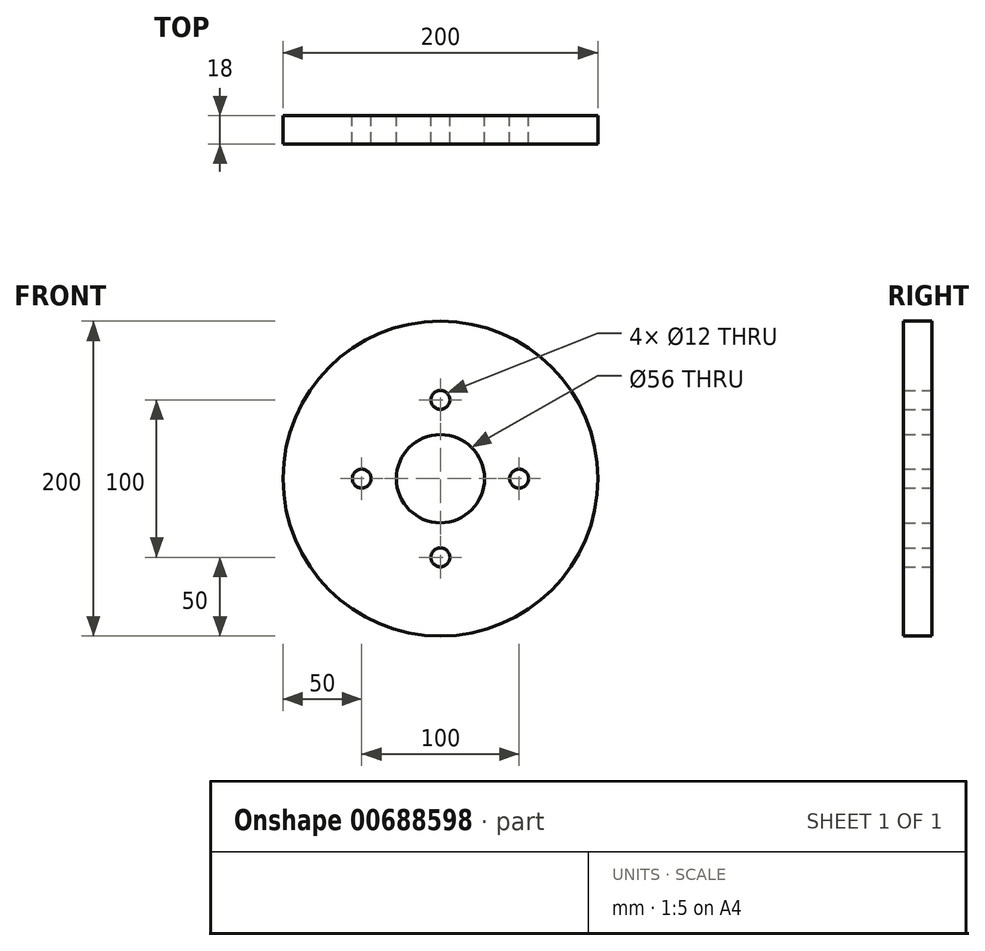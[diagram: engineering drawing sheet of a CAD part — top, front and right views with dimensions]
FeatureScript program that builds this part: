
annotation { "Feature Type Name" : "Feature", "Feature Type Description" : "" }
export const myFeature = defineFeature(function(context is Context, id is Id, definition is map)
    precondition{}
    {
        {
            var Q0;
            Q0=qCreatedBy(makeId("Front.planeOp"),FACE);
            var sketch = newSketch(context, id + "F0", { "sketchPlane" : qUnion([Q0])});
            skCircle(sketch, "E0", {"center": v(0, 0) * mm, "radius": 28 * mm});
            skCircle(sketch, "E1", {"center": v(0, 0) * mm, "radius": 100 * mm});
            skCircle(sketch, "E2.cCircle", {"center": v(0, 0) * mm, "radius": 50 * mm, "construction": true});
            skLineSegment(sketch, "E2.0", {"start": v(50, 50) * mm, "end": v(50, -50) * mm, "construction": true});
            skLineSegment(sketch, "E2.1", {"start": v(50, -50) * mm, "end": v(-50, -50) * mm, "construction": true});
            skLineSegment(sketch, "E2.2", {"start": v(-50, -50) * mm, "end": v(-50, 50) * mm, "construction": true});
            skLineSegment(sketch, "E2.3", {"start": v(-50, 50) * mm, "end": v(50, 50) * mm, "construction": true});
            skPoint(sketch, "E2.0.midPoint", {"position": v(50, 0) * mm});
            skPoint(sketch, "E3", {"position": v(0, 50) * mm});
            skPoint(sketch, "E4", {"position": v(-50, 0) * mm});
            skPoint(sketch, "E5", {"position": v(0, -50) * mm});
            skSolve(sketch);
        }
        {
            var Q0;
            Q0 = qSketchRegion(id + "F0", true);
            extrude(context, id + "F1", {"entities" : qUnion([Q0]), "depth" : 18 * mm, "offsetDistance" : 25 * mm});
        }
        {
            var Q0;
            Q0=sQuery(id+"F0.wireOp",VERTEX,"E3");
            var Q1;
            Q1=sQuery(id+"F0.wireOp",VERTEX,"E2.0.midPoint");
            var Q2;
            Q2=sQuery(id+"F0.wireOp",VERTEX,"E5");
            var Q3;
            Q3=sQuery(id+"F0.wireOp",VERTEX,"E4");
            var Q4;
            Q4=makeQuery(id+"F1.opExtrude","SWEPT_BODY",BODY,{"disambiguationData":[OSD([sQuery(id+"F0.wireOp",EDGE,"E0"),sQuery(id+"F0.wireOp",EDGE,"E1")])]});
            hole(context, id + "F2", {"style" : HoleStyle.SIMPLE, "endStyle" : HoleEndStyle.THROUGH, "oppositeDirection" : true, "holeDiameter" : 12 * mm, "majorDiameter" : 5 * mm, "isTappedThrough" : true, "tappedDepth" : 12 * mm, "tapClearance" : 3, "locations" : qUnion([Q0, Q1, Q2, Q3]), "scope" : qUnion([Q4])});
        }
        {
            var Q0;
            Q0=makeQuery(id+"F1.opExtrude","CAP_FACE",FACE,{"disambiguationData":[OSD([sQuery(id+"F0.wireOp",EDGE,"E0"),sQuery(id+"F0.wireOp",EDGE,"E1")])],"isStart":false});
            var sketch = newSketch(context, id + "F3", { "sketchPlane" : qUnion([Q0])});
            skCircle(sketch, "E6.cCircle", {"center": v(0, 0) * mm, "radius": 57.15 * mm, "construction": true});
            skLineSegment(sketch, "E6.0", {"start": v(-0.38, 70.64) * mm, "end": v(67.06, 22.2) * mm, "construction": true});
            skLineSegment(sketch, "E6.1", {"start": v(67.06, 22.2) * mm, "end": v(41.83, -56.92) * mm, "construction": true});
            skLineSegment(sketch, "E6.2", {"start": v(41.83, -56.92) * mm, "end": v(-41.21, -57.37) * mm, "construction": true});
            skLineSegment(sketch, "E6.3", {"start": v(-41.21, -57.37) * mm, "end": v(-67.3, 21.47) * mm, "construction": true});
            skLineSegment(sketch, "E6.4", {"start": v(-67.3, 21.47) * mm, "end": v(-0.38, 70.64) * mm, "construction": true});
            skPoint(sketch, "E6.0.midPoint", {"position": v(33.34, 46.42) * mm});
            skPoint(sketch, "E7", {"position": v(-33.84, 46.05) * mm});
            skPoint(sketch, "E8", {"position": v(54.45, -17.37) * mm});
            skPoint(sketch, "E9", {"position": v(0.3, -57.15) * mm});
            skPoint(sketch, "E10", {"position": v(-54.26, -17.95) * mm});
            skSolve(sketch);
        }
    });
